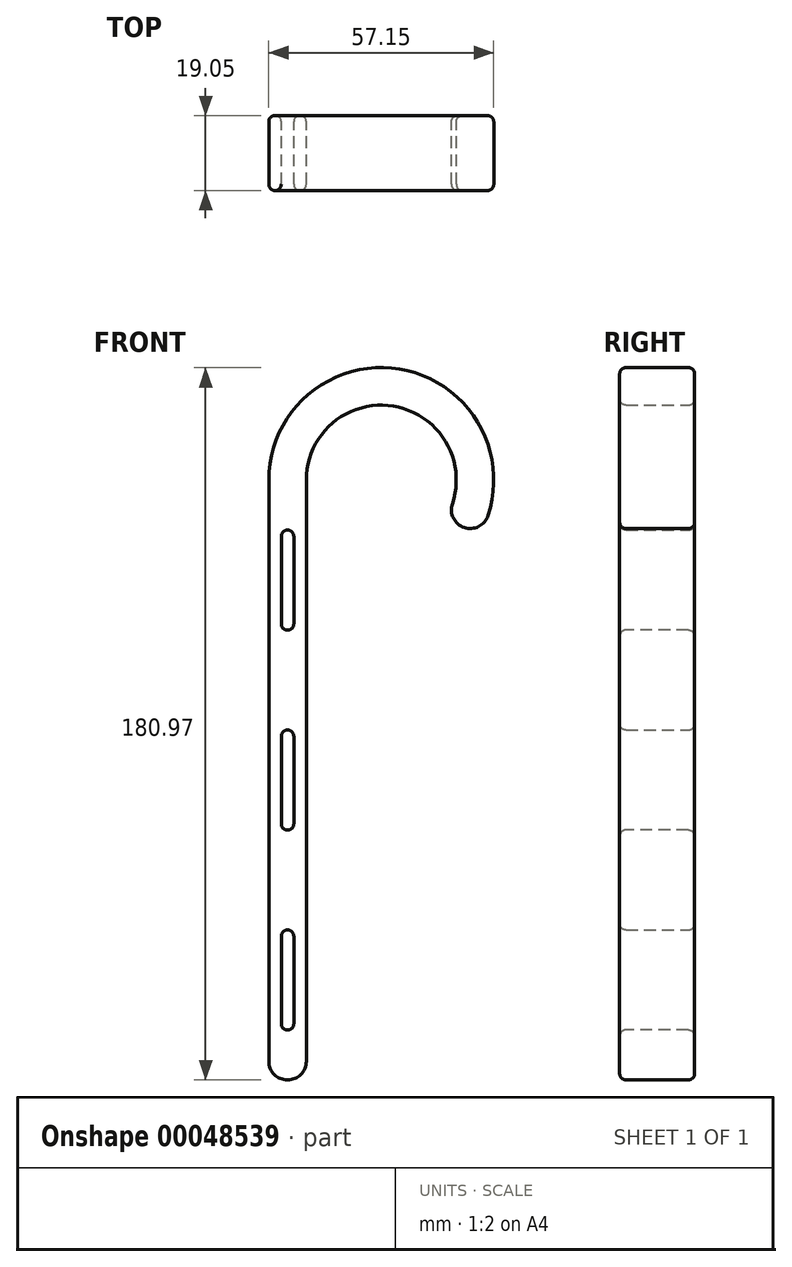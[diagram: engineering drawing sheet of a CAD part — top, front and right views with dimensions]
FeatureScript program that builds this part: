
annotation { "Feature Type Name" : "Feature", "Feature Type Description" : "" }
export const myFeature = defineFeature(function(context is Context, id is Id, definition is map)
    precondition{}
    {
        {
            var Q0;
            Q0=qCreatedBy(makeId("Front.planeOp"),FACE);
            var sketch = newSketch(context, id + "F0", { "sketchPlane" : qUnion([Q0])});
            skLineSegment(sketch, "E0", {"start": v(-40, 0) * mm, "end": v(-40, -152.4) * mm});
            skArc(sketch, "E1", {"start": v(-40, 0) * mm, "mid": v(-11.43, 28.58) * mm, "end": v(17.15, 0) * mm});
            skLineSegment(sketch, "E2", {"start": v(-30.48, 0) * mm, "end": v(-30.48, -152.4) * mm});
            skLineSegment(sketch, "E3", {"start": v(-30.48, 0) * mm, "end": v(-30.48, 0) * mm});
            skLineSegment(sketch, "E4", {"start": v(-11.43, 0) * mm, "end": v(-11.43, -152.4) * mm, "construction": true});
            skLineSegment(sketch, "E5", {"start": v(-11.43, 0) * mm, "end": v(23.13, -19.95) * mm, "construction": true});
            skArc(sketch, "E6", {"start": v(-30.48, 0) * mm, "mid": v(-6.5, 18.4) * mm, "end": v(5.07, -9.52) * mm});
            skArc(sketch, "E7", {"start": v(17.15, 0) * mm, "mid": v(16.17, -7.4) * mm, "end": v(13.32, -14.29) * mm});
            skLineSegment(sketch, "E8", {"start": v(5.07, -9.52) * mm, "end": v(13.32, -14.29) * mm});
            skLineSegment(sketch, "E9", {"start": v(-30.48, -152.4) * mm, "end": v(-40, -152.4) * mm});
            skLineSegment(sketch, "E10", {"start": v(-35.24, -152.4) * mm, "end": v(-35.24, 0) * mm, "construction": true});
            skLineSegment(sketch, "E11.bottom", {"start": v(-36.83, -139.7) * mm, "end": v(-33.65, -139.7) * mm});
            skLineSegment(sketch, "E11.top", {"start": v(-36.83, -114.3) * mm, "end": v(-33.65, -114.3) * mm});
            skLineSegment(sketch, "E11.left", {"start": v(-36.83, -139.7) * mm, "end": v(-36.83, -114.3) * mm});
            skLineSegment(sketch, "E11.right", {"start": v(-33.65, -139.7) * mm, "end": v(-33.65, -114.3) * mm});
            skPoint(sketch, "E11.middle", {"position": v(-35.24, -127) * mm});
            skLineSegment(sketch, "E12.bottom", {"start": v(-36.83, -88.9) * mm, "end": v(-33.65, -88.9) * mm});
            skLineSegment(sketch, "E12.top", {"start": v(-36.83, -63.5) * mm, "end": v(-33.65, -63.5) * mm});
            skLineSegment(sketch, "E12.left", {"start": v(-36.83, -88.9) * mm, "end": v(-36.83, -63.5) * mm});
            skLineSegment(sketch, "E12.right", {"start": v(-33.65, -88.9) * mm, "end": v(-33.65, -63.5) * mm});
            skPoint(sketch, "E12.middle", {"position": v(-35.24, -76.2) * mm});
            skLineSegment(sketch, "E13.bottom", {"start": v(-36.83, -38.1) * mm, "end": v(-33.66, -38.1) * mm});
            skLineSegment(sketch, "E13.top", {"start": v(-36.83, -12.7) * mm, "end": v(-33.66, -12.7) * mm});
            skLineSegment(sketch, "E13.left", {"start": v(-36.83, -38.1) * mm, "end": v(-36.83, -12.7) * mm});
            skLineSegment(sketch, "E13.right", {"start": v(-33.66, -38.1) * mm, "end": v(-33.66, -12.7) * mm});
            skPoint(sketch, "E13.middle", {"position": v(-35.24, -25.4) * mm});
            skSolve(sketch);
        }
        {
            var Q0;
            Q0=makeQuery(id+"F0.imprint","IMPRINT",FACE,{"disambiguationData":[TD([[makeQuery(id+"F0.imprint","IMPRINT",EDGE,{"derivedFrom":sQuery(id+"F0.wireOp",EDGE,"E0")}),1.0]])]});
            var Q1;
            Q1=makeQuery(id+"F0.imprint","IMPRINT",FACE,{"disambiguationData":[TD([[makeQuery(id+"F0.imprint","IMPRINT",EDGE,{"derivedFrom":sQuery(id+"F0.wireOp",EDGE,"qGwicptO-gK2j-Kfag-Chg2-fPSLUECn81Ir")}),1.0]])]});
            var Q2;
            Q2=makeQuery(id+"F0.imprint","IMPRINT",FACE,{"disambiguationData":[TD([[makeQuery(id+"F0.imprint","IMPRINT",EDGE,{"derivedFrom":sQuery(id+"F0.wireOp",EDGE,"xNmMEBZU-oUyY-ZiBH-kAaP-bqtLUd6SUk8f")}),1.0]])]});
            extrude(context, id + "F1", {"entities" : qUnion([Q0, Q1, Q2]), "depth" : 19.05 * mm, "offsetDistance" : 25.4 * mm});
        }
        {
            var Q0;
            Q0=makeQuery(id+"F1.opExtrude","SWEPT_EDGE",EDGE,{"disambiguationData":[OSD([sQuery(id+"F0.wireOp",EDGE,"E7"),sQuery(id+"F0.wireOp",EDGE,"E8")])]});
            var Q1;
            Q1=makeQuery(id+"F1.opExtrude","SWEPT_EDGE",EDGE,{"disambiguationData":[OSD([sQuery(id+"F0.wireOp",EDGE,"E6"),sQuery(id+"F0.wireOp",EDGE,"E8")])]});
            var Q2;
            Q2=makeQuery(id+"F1.opExtrude","SWEPT_EDGE",EDGE,{"disambiguationData":[OSD([sQuery(id+"F0.wireOp",EDGE,"E2"),sQuery(id+"F0.wireOp",EDGE,"E9")])]});
            var Q3;
            Q3=makeQuery(id+"F1.opExtrude","SWEPT_EDGE",EDGE,{"disambiguationData":[OSD([sQuery(id+"F0.wireOp",EDGE,"E0"),sQuery(id+"F0.wireOp",EDGE,"E9")])]});
            fillet(context, id + "F2", {"entities" : qUnion([Q0, Q1, Q2, Q3]), "tangentPropagation" : true, "radius" : 4.76 * mm, "defaultsChanged" : false, "vertexSettings" : [], "allowEdgeOverflow" : false});
        }
        {
            var Q0;
            Q0=makeQuery(id+"F1.opExtrude","SWEPT_FACE",FACE,{"disambiguationData":[OSD([sQuery(id+"F0.wireOp",EDGE,"E13.top")])]});
            var Q1;
            Q1=makeQuery(id+"F1.opExtrude","SWEPT_FACE",FACE,{"disambiguationData":[OSD([sQuery(id+"F0.wireOp",EDGE,"E12.top")])]});
            var Q2;
            Q2=makeQuery(id+"F1.opExtrude","SWEPT_FACE",FACE,{"disambiguationData":[OSD([sQuery(id+"F0.wireOp",EDGE,"E11.top")])]});
            var Q3;
            Q3=makeQuery(id+"F1.opExtrude","SWEPT_FACE",FACE,{"disambiguationData":[OSD([sQuery(id+"F0.wireOp",EDGE,"E11.bottom")])]});
            var Q4;
            Q4=makeQuery(id+"F1.opExtrude","SWEPT_FACE",FACE,{"disambiguationData":[OSD([sQuery(id+"F0.wireOp",EDGE,"E12.bottom")])]});
            var Q5;
            Q5=makeQuery(id+"F1.opExtrude","SWEPT_FACE",FACE,{"disambiguationData":[OSD([sQuery(id+"F0.wireOp",EDGE,"E13.bottom")])]});
            fillet(context, id + "F3", {"entities" : qUnion([Q0, Q1, Q2, Q3, Q4, Q5]), "tangentPropagation" : true, "radius" : 1.59 * mm, "defaultsChanged" : false, "vertexSettings" : [], "allowEdgeOverflow" : false});
        }
        {
            var Q0;
            Q0=makeQuery(id+"F1.opExtrude","CAP_FACE",FACE,{"disambiguationData":[OSD([sQuery(id+"F0.wireOp",EDGE,"E0"),sQuery(id+"F0.wireOp",EDGE,"E1"),sQuery(id+"F0.wireOp",EDGE,"E2"),sQuery(id+"F0.wireOp",EDGE,"E6"),sQuery(id+"F0.wireOp",EDGE,"E7"),sQuery(id+"F0.wireOp",EDGE,"E8"),sQuery(id+"F0.wireOp",EDGE,"E9"),sQuery(id+"F0.wireOp",EDGE,"E11.bottom"),sQuery(id+"F0.wireOp",EDGE,"E11.top"),sQuery(id+"F0.wireOp",EDGE,"E11.left"),sQuery(id+"F0.wireOp",EDGE,"E11.right"),sQuery(id+"F0.wireOp",EDGE,"E12.bottom"),sQuery(id+"F0.wireOp",EDGE,"E12.top"),sQuery(id+"F0.wireOp",EDGE,"E12.left"),sQuery(id+"F0.wireOp",EDGE,"E12.right"),sQuery(id+"F0.wireOp",EDGE,"E13.bottom"),sQuery(id+"F0.wireOp",EDGE,"E13.top"),sQuery(id+"F0.wireOp",EDGE,"E13.left"),sQuery(id+"F0.wireOp",EDGE,"E13.right")])],"isStart":false});
            var Q1;
            Q1=makeQuery(id+"F1.opExtrude","CAP_FACE",FACE,{"disambiguationData":[OSD([sQuery(id+"F0.wireOp",EDGE,"E0"),sQuery(id+"F0.wireOp",EDGE,"E1"),sQuery(id+"F0.wireOp",EDGE,"E2"),sQuery(id+"F0.wireOp",EDGE,"E6"),sQuery(id+"F0.wireOp",EDGE,"E7"),sQuery(id+"F0.wireOp",EDGE,"E8"),sQuery(id+"F0.wireOp",EDGE,"E9"),sQuery(id+"F0.wireOp",EDGE,"E11.bottom"),sQuery(id+"F0.wireOp",EDGE,"E11.top"),sQuery(id+"F0.wireOp",EDGE,"E11.left"),sQuery(id+"F0.wireOp",EDGE,"E11.right"),sQuery(id+"F0.wireOp",EDGE,"E12.bottom"),sQuery(id+"F0.wireOp",EDGE,"E12.top"),sQuery(id+"F0.wireOp",EDGE,"E12.left"),sQuery(id+"F0.wireOp",EDGE,"E12.right"),sQuery(id+"F0.wireOp",EDGE,"E13.bottom"),sQuery(id+"F0.wireOp",EDGE,"E13.top"),sQuery(id+"F0.wireOp",EDGE,"E13.left"),sQuery(id+"F0.wireOp",EDGE,"E13.right")])],"isStart":true});
            fillet(context, id + "F4", {"entities" : qUnion([Q0, Q1]), "tangentPropagation" : true, "radius" : 1.59 * mm, "defaultsChanged" : false, "vertexSettings" : [], "allowEdgeOverflow" : false});
        }
    });
